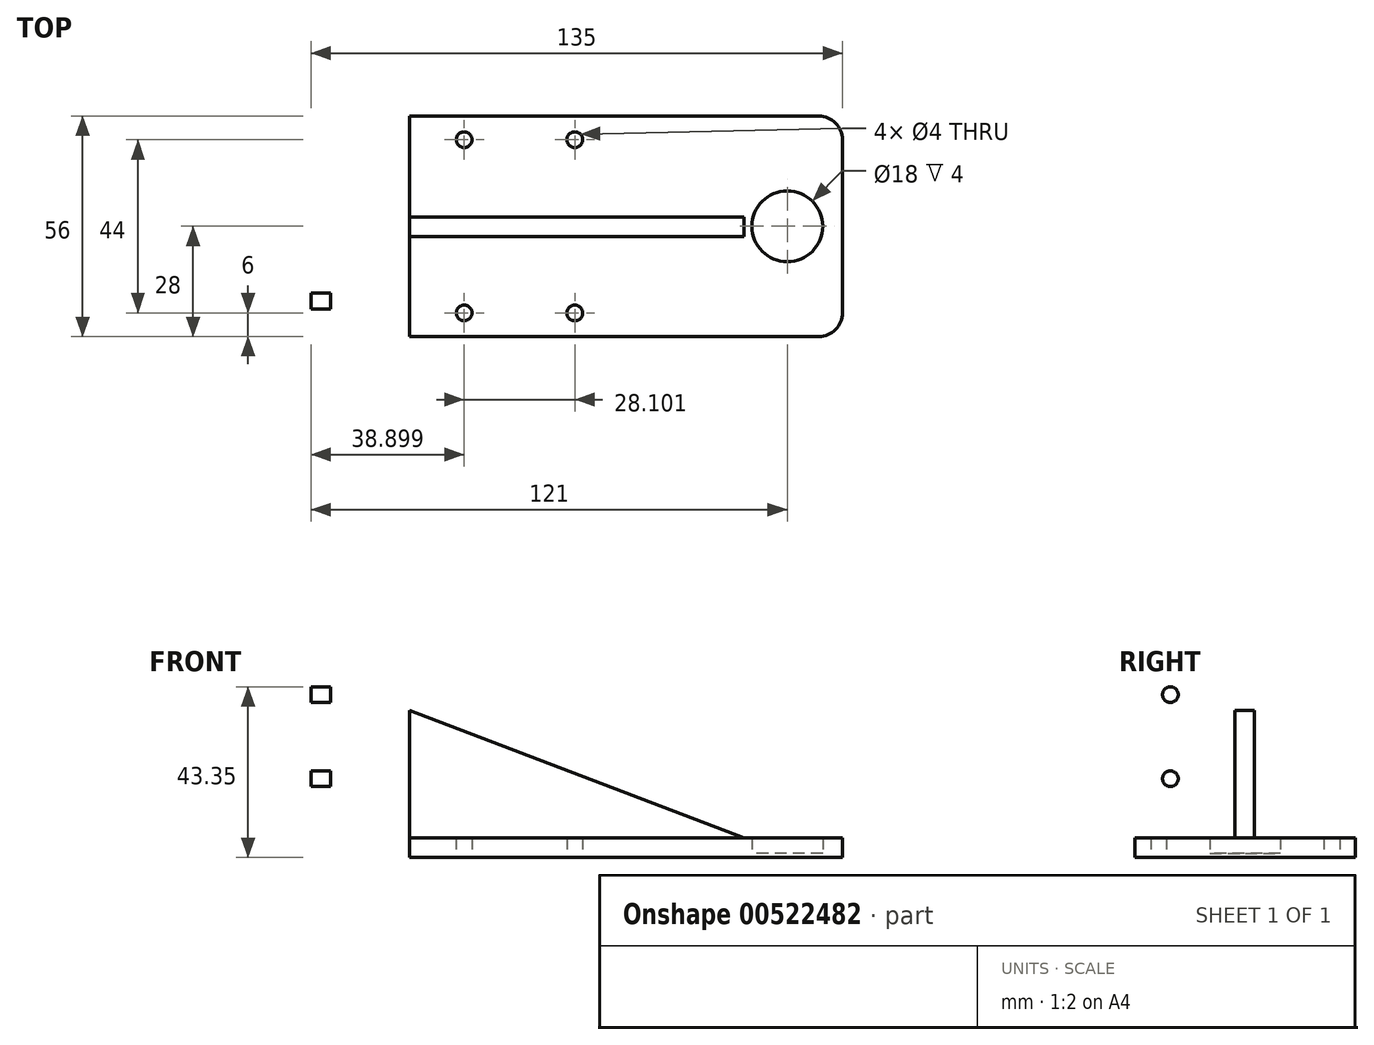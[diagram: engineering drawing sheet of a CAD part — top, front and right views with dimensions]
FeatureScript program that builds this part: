
annotation { "Feature Type Name" : "Feature", "Feature Type Description" : "" }
export const myFeature = defineFeature(function(context is Context, id is Id, definition is map)
    precondition{}
    {
        {
            var Q0;
            Q0=qCreatedBy(makeId("Top.planeOp"),FACE);
            var sketch = newSketch(context, id + "F0", { "sketchPlane" : qUnion([Q0])});
            skLineSegment(sketch, "E0.bottom", {"start": v(65, -28) * mm, "end": v(-65, -28) * mm});
            skLineSegment(sketch, "E0.top", {"start": v(65, 28) * mm, "end": v(-65, 28) * mm});
            skLineSegment(sketch, "E0.left", {"start": v(65, -28) * mm, "end": v(65, 28) * mm});
            skLineSegment(sketch, "E0.right", {"start": v(-65, -28) * mm, "end": v(-65, 28) * mm});
            skPoint(sketch, "E0.middle", {"position": v(0, 0) * mm});
            skLineSegment(sketch, "E1.bottom", {"start": v(-65, 28) * mm, "end": v(-70, 28) * mm});
            skLineSegment(sketch, "E1.top", {"start": v(-65, -28) * mm, "end": v(-70, -28) * mm});
            skLineSegment(sketch, "E1.left", {"start": v(-65, 28) * mm, "end": v(-65, -28) * mm});
            skLineSegment(sketch, "E1.right", {"start": v(-70, 28) * mm, "end": v(-70, -28) * mm});
            skCircle(sketch, "E2", {"center": v(51, 0) * mm, "radius": 9 * mm});
            skCircle(sketch, "E3", {"center": v(-3, 22) * mm, "radius": 2 * mm});
            skCircle(sketch, "E4", {"center": v(-31.1, 22) * mm, "radius": 2 * mm});
            skCircle(sketch, "E5.MirrorC", {"center": v(-3, -22) * mm, "radius": 2 * mm});
            skCircle(sketch, "E6.MirrorC", {"center": v(-31.1, -22) * mm, "radius": 2 * mm});
            skLineSegment(sketch, "E7.bottom", {"start": v(-65, 2.36) * mm, "end": v(40, 2.36) * mm});
            skLineSegment(sketch, "E7.top", {"start": v(-65, -2.64) * mm, "end": v(40, -2.64) * mm});
            skLineSegment(sketch, "E7.left", {"start": v(-65, 2.36) * mm, "end": v(-65, -2.64) * mm});
            skLineSegment(sketch, "E7.right", {"start": v(40, 2.36) * mm, "end": v(40, -2.64) * mm});
            skSolve(sketch);
        }
        {
            var Q0;
            Q0=makeQuery(id+"F0.imprint","IMPRINT",FACE,{"disambiguationData":[TD([[makeQuery(id+"F0.imprint","IMPRINT",EDGE,{"derivedFrom":sQuery(id+"F0.wireOp",EDGE,"E1.bottom")}),1.0]])]});
            extrude(context, id + "F1", {"entities" : qUnion([Q0]), "depth" : 50 * mm, "offsetDistance" : 25 * mm});
        }
        {
            var Q0;
            Q0=makeQuery(id+"F0.imprint","IMPRINT",FACE,{"disambiguationData":[TD([[makeQuery(id+"F0.imprint","IMPRINT",EDGE,{"derivedFrom":sQuery(id+"F0.wireOp",EDGE,"E0.bottom")}),-1.0]])]});
            extrude(context, id + "F2", {"entities" : qUnion([Q0]), "operationType" : NewBodyOperationType.ADD, "depth" : 5 * mm, "offsetDistance" : 25 * mm});
        }
        {
            var Q0;
            Q0=makeQuery(id+"F1.opExtrude","CAP_EDGE",EDGE,{"disambiguationData":[OSD([sQuery(id+"F0.wireOp",EDGE,"E1.bottom")])],"isStart":false});
            var Q1;
            Q1=makeQuery(id+"F1.opExtrude","CAP_EDGE",EDGE,{"disambiguationData":[OSD([sQuery(id+"F0.wireOp",EDGE,"E1.top")])],"isStart":false});
            var Q2;
            Q2=makeQuery(id+"F2.opExtrude","SWEPT_EDGE",EDGE,{"disambiguationData":[OSD([sQuery(id+"F0.wireOp",EDGE,"E0.bottom"),sQuery(id+"F0.wireOp",EDGE,"E0.left")])]});
            var Q3;
            Q3=makeQuery(id+"F2.opExtrude","SWEPT_EDGE",EDGE,{"disambiguationData":[OSD([sQuery(id+"F0.wireOp",EDGE,"E0.top"),sQuery(id+"F0.wireOp",EDGE,"E0.left")])]});
            var Q4;
            Q4=makeQuery(id+"F2.opExtrude","CAP_EDGE",EDGE,{"disambiguationData":[OSD([sQuery(id+"F0.wireOp",EDGE,"E1.left")])],"isStart":false});
            fillet(context, id + "F3", {"entities" : qUnion([Q0, Q1, Q2, Q3, Q4]), "radius" : 6 * mm, "tangentPropagation" : true, "allowEdgeOverflow" : false});
        }
        {
            var Q0;
            Q0=makeQuery(id+"F0.imprint","IMPRINT",FACE,{"disambiguationData":[TD([[makeQuery(id+"F0.imprint","IMPRINT",EDGE,{"derivedFrom":sQuery(id+"F0.wireOp",EDGE,"E2")}),1.0]])]});
            extrude(context, id + "F4", {"entities" : qUnion([Q0]), "operationType" : NewBodyOperationType.ADD, "depth" : 1 * mm, "offsetDistance" : 25 * mm});
        }
        {
            var Q0;
            Q0=makeQuery(id+"F0.imprint","IMPRINT",FACE,{"disambiguationData":[TD([[makeQuery(id+"F0.imprint","IMPRINT",EDGE,{"derivedFrom":sQuery(id+"F0.wireOp",EDGE,"E7.bottom")}),-1.0]])]});
            extrude(context, id + "F5", {"entities" : qUnion([Q0]), "operationType" : NewBodyOperationType.ADD, "depth" : 45 * mm, "offsetDistance" : 25 * mm});
        }
        {
            var Q0;
            Q0=makeQuery(id+"F5.opExtrude","SWEPT_FACE",FACE,{"disambiguationData":[OSD([sQuery(id+"F0.wireOp",EDGE,"E7.top")])]});
            var sketch = newSketch(context, id + "F6", { "sketchPlane" : qUnion([Q0])});
            skLineSegment(sketch, "E8", {"start": v(-65, 45) * mm, "end": v(40, 5) * mm});
            skSolve(sketch);
        }
        {
            var Q0;
            Q0=makeQuery(id+"F6.imprint","IMPRINT",FACE,{"disambiguationData":[TD([[makeQuery(id+"F6.imprint","IMPRINT",EDGE,{"derivedFrom":sQuery(id+"F6.wireOp",EDGE,"E8")}),1.0]])]});
            extrude(context, id + "F7", {"entities" : qUnion([Q0]), "operationType" : NewBodyOperationType.REMOVE, "oppositeDirection" : true, "depth" : 25 * mm, "offsetDistance" : 25 * mm});
        }
        {
            var Q0;
            Q0=makeQuery(id+"F1.opExtrude","SWEPT_FACE",FACE,{"disambiguationData":[OSD([sQuery(id+"F0.wireOp",EDGE,"E1.right")])]});
            var sketch = newSketch(context, id + "F8", { "sketchPlane" : qUnion([Q0])});
            skCircle(sketch, "E9", {"center": v(-19, 41.35) * mm, "radius": 2 * mm});
            skCircle(sketch, "E10", {"center": v(-19, 20) * mm, "radius": 2 * mm});
            skCircle(sketch, "E11.MirrorC", {"center": v(19, 20) * mm, "radius": 2 * mm});
            skCircle(sketch, "E12.MirrorC", {"center": v(19, 41.35) * mm, "radius": 2 * mm});
            skSolve(sketch);
        }
        {
            var Q0;
            Q0=makeQuery(id+"F8.imprint","IMPRINT",FACE,{"disambiguationData":[TD([[makeQuery(id+"F8.imprint","IMPRINT",EDGE,{"derivedFrom":sQuery(id+"F8.wireOp",EDGE,"E9")}),1.0]])]});
            var Q1;
            Q1=makeQuery(id+"F8.imprint","IMPRINT",FACE,{"disambiguationData":[TD([[makeQuery(id+"F8.imprint","IMPRINT",EDGE,{"derivedFrom":sQuery(id+"F8.wireOp",EDGE,"E10")}),1.0]])]});
            var Q2;
            Q2=makeQuery(id+"F8.imprint","IMPRINT",FACE,{"disambiguationData":[TD([[makeQuery(id+"F8.imprint","IMPRINT",EDGE,{"derivedFrom":sQuery(id+"F8.wireOp",EDGE,"E12.MirrorC")}),-1.0]])]});
            var Q3;
            Q3=makeQuery(id+"F8.imprint","IMPRINT",FACE,{"disambiguationData":[TD([[makeQuery(id+"F8.imprint","IMPRINT",EDGE,{"derivedFrom":sQuery(id+"F8.wireOp",EDGE,"E11.MirrorC")}),-1.0]])]});
            extrude(context, id + "F9", {"entities" : qUnion([Q0, Q1, Q2, Q3]), "operationType" : NewBodyOperationType.REMOVE, "oppositeDirection" : true, "depth" : 25 * mm, "offsetDistance" : 25 * mm});
        }
    });
